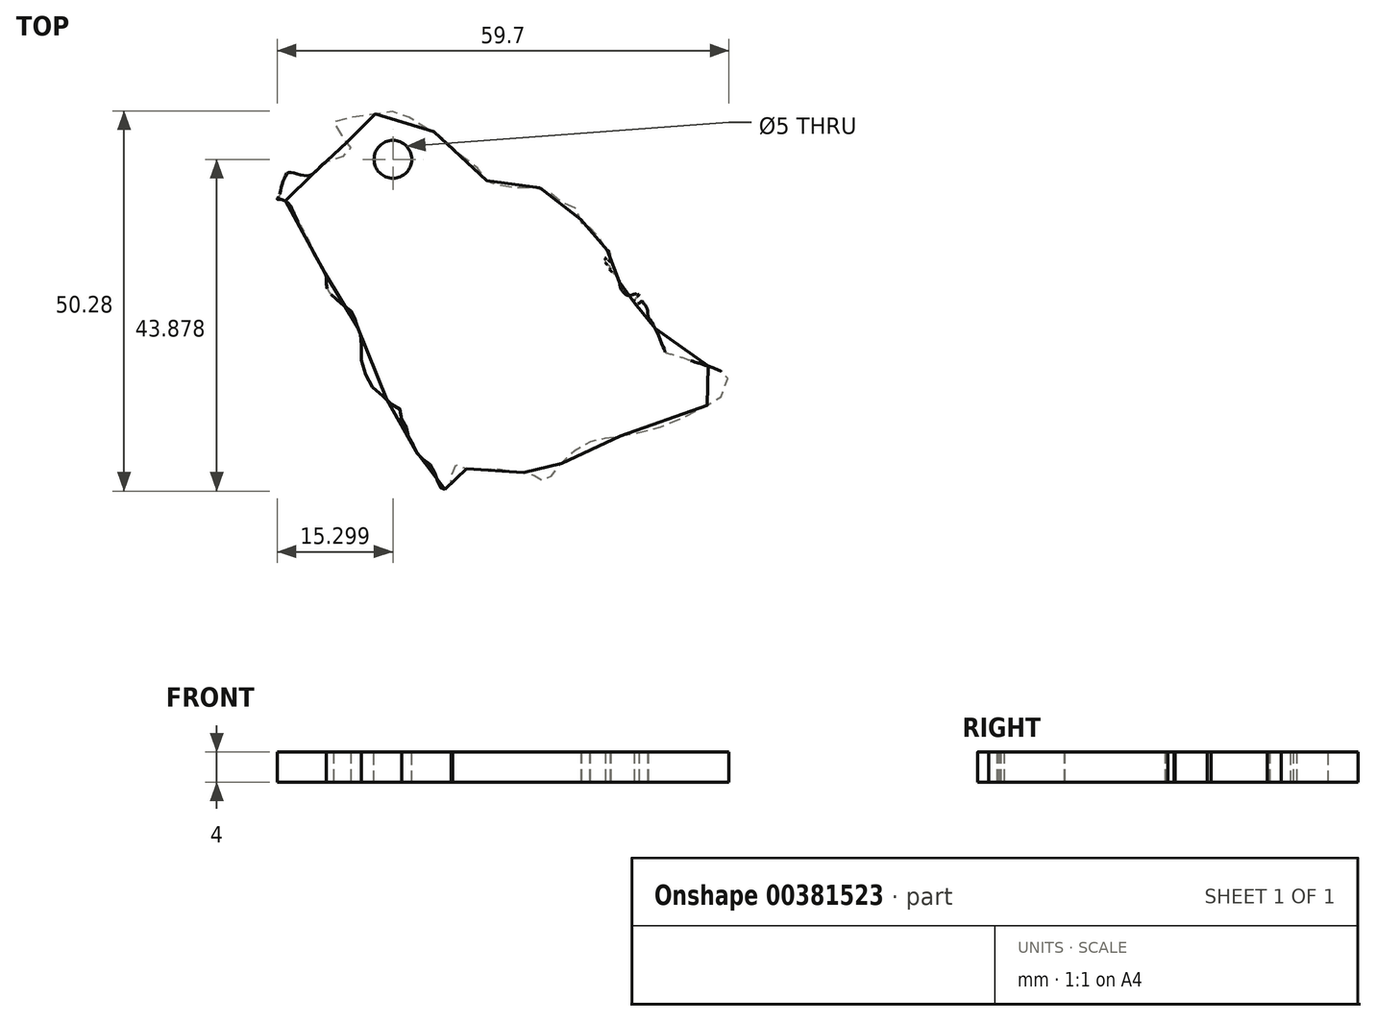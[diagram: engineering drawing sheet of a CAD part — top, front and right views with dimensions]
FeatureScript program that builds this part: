
annotation { "Feature Type Name" : "Feature", "Feature Type Description" : "" }
export const myFeature = defineFeature(function(context is Context, id is Id, definition is map)
    precondition{}
    {
        {
            var Q0;
            Q0=qCreatedBy(makeId("Top.planeOp"),FACE);
            var sketch = newSketch(context, id + "F0", { "sketchPlane" : qUnion([Q0])});
            skLineSegment(sketch, "E0", {"start": v(31.35, 26.38) * mm, "end": v(-28.65, -24.1) * mm, "construction": true});
            skFitSpline(sketch, "E1", {"points": [v(-6.3, -23.73) * mm, v(-6.16, -23.58) * mm, v(-6, -23.43) * mm, v(-5.79, -23.35) * mm, v(-5.6, -23.24) * mm, v(-5.48, -23.15) * mm, v(-5.57, -22.91) * mm, v(-5.62, -22.62) * mm, v(-5.63, -22.36) * mm, v(-5.51, -22.1) * mm, v(-5.34, -22) * mm, v(-5.37, -21.68) * mm, v(-5.4, -21.39) * mm, v(-5.37, -21.04) * mm, v(-5.27, -20.71) * mm, v(-5.05, -20.55) * mm, v(-4.8, -20.49) * mm, v(-4.56, -20.5) * mm, v(-4.28, -20.6) * mm, v(-3.95, -20.76) * mm, v(-3.66, -20.91) * mm, v(-3.34, -21.03) * mm, v(-2.93, -21.12) * mm, v(-2.37, -21.15) * mm, v(-1.75, -21.1) * mm, v(-1.23, -21.01) * mm, v(-0.67, -21) * mm, v(-0.25, -20.93) * mm, v(0.26, -20.95) * mm, v(0.85, -21) * mm, v(1.25, -21.08) * mm, v(1.93, -21.28) * mm, v(2.47, -21.36) * mm, v(2.88, -21.45) * mm, v(3.24, -21.44) * mm, v(3.67, -21.45) * mm, v(4.15, -21.5) * mm, v(4.52, -21.54) * mm, v(4.8, -21.58) * mm, v(5.1, -21.68) * mm, v(5.3, -21.8) * mm, v(5.6, -21.97) * mm, v(5.77, -22.08) * mm, v(5.87, -22.15) * mm, v(6, -22.23) * mm, v(6.13, -22.32) * mm, v(6.34, -22.43) * mm, v(6.59, -22.49) * mm, v(6.8, -22.5) * mm, v(7.05, -22.48) * mm, v(7.3, -22.36) * mm, v(7.6, -22.12) * mm, v(7.82, -21.88) * mm, v(8.05, -21.57) * mm, v(8.34, -21.16) * mm, v(8.86, -20.5) * mm, v(9.34, -20.02) * mm, v(9.9, -19.43) * mm, v(10.7, -18.66) * mm, v(11.79, -17.89) * mm, v(12.38, -17.61) * mm, v(12.95, -17.38) * mm, v(13.53, -17.2) * mm, v(14, -17.1) * mm, v(14.57, -17) * mm, v(15.02, -16.93) * mm, v(15.35, -16.86) * mm, v(15.89, -16.77) * mm, v(16.56, -16.7) * mm, v(16.9, -16.65) * mm, v(17.4, -16.56) * mm, v(17.75, -16.5) * mm, v(19.49, -16.2) * mm, v(20.7, -15.9) * mm, v(21.96, -15.55) * mm, v(23.1, -15.14) * mm, v(25.05, -14.28) * mm, v(26.33, -13.68) * mm, v(27.58, -13.04) * mm, v(28.64, -12.48) * mm, v(29.67, -12.08) * mm, v(30.02, -11.8) * mm, v(30.4, -11.13) * mm, v(30.69, -10.26) * mm, v(30.98, -9.29) * mm, v(31.19, -8.8) * mm, v(31.19, -8.62) * mm, v(30.94, -8.48) * mm, v(30.56, -8.31) * mm, v(30.26, -8.15) * mm, v(29.83, -7.94) * mm, v(29.5, -7.78) * mm, v(29.19, -7.66) * mm, v(28.73, -7.5) * mm, v(28.33, -7.38) * mm, v(27.85, -7.24) * mm, v(27.52, -7.11) * mm, v(27.18, -7) * mm, v(26.27, -6.74) * mm, v(25.29, -6.4) * mm, v(23.78, -5.95) * mm, v(22.84, -5.64) * mm, v(22.78, -5.51) * mm, v(22.66, -5.17) * mm, v(22.44, -4.7) * mm, v(22.14, -4.05) * mm, v(21.82, -3.17) * mm, v(21.44, -2.35) * mm, v(21.17, -1.9) * mm, v(21, -1.58) * mm, v(20.75, -1.2) * mm, v(20.52, -1.04) * mm, v(20.56, -0.68) * mm, v(20.46, -0.22) * mm, v(20.46, 0) * mm, v(20.39, 0.16) * mm, v(20.27, 0.4) * mm, v(20.19, 0.58) * mm, v(20.07, 0.68) * mm, v(20, 0.77) * mm, v(19.94, 0.9) * mm, v(19.9, 0.99) * mm, v(19.8, 1.1) * mm, v(19.73, 1.16) * mm, v(19.61, 1.13) * mm, v(19.54, 1.06) * mm, v(19.39, 0.91) * mm, v(19.2, 0.82) * mm, v(19.04, 0.78) * mm, v(18.83, 0.84) * mm, v(18.74, 0.93) * mm, v(18.71, 1.1) * mm, v(18.7, 1.3) * mm, v(18.8, 1.4) * mm, v(19.04, 1.66) * mm, v(19.17, 1.8) * mm, v(19.36, 2.06) * mm, v(19.25, 2.03) * mm, v(19.14, 2) * mm, v(19.03, 2.01) * mm, v(18.96, 2.08) * mm, v(18.94, 2.13) * mm, v(18.84, 2.14) * mm, v(18.7, 2.08) * mm, v(18.56, 2.02) * mm, v(18.38, 1.96) * mm, v(18.22, 1.93) * mm, v(18.1, 1.92) * mm, v(17.9, 1.94) * mm, v(17.65, 2.02) * mm, v(17.38, 2.24) * mm, v(17.1, 2.56) * mm, v(16.9, 2.92) * mm, v(16.82, 3.24) * mm, v(16.74, 3.75) * mm, v(16.54, 4.25) * mm, v(16.22, 4.65) * mm, v(15.76, 5.04) * mm, v(15.53, 5.27) * mm, v(15.54, 5.6) * mm, v(15.48, 5.8) * mm, v(15.19, 5.91) * mm, v(14.99, 6.18) * mm, v(14.9, 6.74) * mm, v(14.94, 6.9) * mm, v(15.14, 6.71) * mm, v(15.36, 6.51) * mm, v(15.52, 6.42) * mm, v(15.57, 6.7) * mm, v(15.59, 7.04) * mm, v(15.59, 7.34) * mm, v(15.47, 7.67) * mm, v(15.23, 7.88) * mm, v(15.04, 8.01) * mm, v(14.94, 8.12) * mm, v(14.9, 8.24) * mm, v(14.88, 8.43) * mm, v(14.83, 8.64) * mm, v(14.67, 9) * mm, v(14.27, 9.42) * mm, v(13.88, 9.8) * mm, v(13.47, 10.17) * mm, v(13.1, 10.42) * mm, v(12.88, 10.55) * mm, v(12.8, 10.63) * mm, v(12.86, 10.91) * mm, v(12.84, 11.05) * mm, v(12.76, 11.13) * mm, v(12.64, 11.16) * mm, v(12.44, 11.19) * mm, v(12.2, 11.21) * mm, v(12.05, 11.27) * mm, v(11.9, 11.35) * mm, v(11.69, 11.66) * mm, v(11.69, 12.1) * mm, v(11.53, 12.54) * mm, v(11.12, 13.04) * mm, v(10.8, 13.7) * mm, v(10.56, 14.1) * mm, v(10.43, 14.3) * mm, v(9.9, 14.3) * mm, v(9.2, 14.24) * mm, v(8.7, 14.2) * mm, v(8.17, 14.42) * mm, v(7.82, 14.83) * mm, v(7.54, 15.46) * mm, v(7.35, 15.77) * mm, v(7.1, 16) * mm, v(6.63, 16.15) * mm, v(6.03, 16.15) * mm, v(5.4, 16.15) * mm, v(4.75, 16.13) * mm, v(4.12, 16.12) * mm, v(3.57, 16.11) * mm, v(3.02, 16.12) * mm, v(2.41, 16.13) * mm, v(2.06, 16.18) * mm, v(1.56, 16.25) * mm, v(0.95, 16.43) * mm, v(0.5, 16.58) * mm, v(0.17, 16.7) * mm, v(0.06, 16.74) * mm, v(-0.08, 16.8) * mm, v(-0.3, 16.87) * mm, v(-0.5, 16.94) * mm, v(-0.7, 17) * mm, v(-0.8, 17.2) * mm, v(-0.99, 17.5) * mm, v(-1.3, 17.9) * mm, v(-1.84, 18.58) * mm, v(-2.6, 19.25) * mm, v(-3.47, 19.91) * mm, v(-4.24, 20.48) * mm, v(-5.04, 21.1) * mm, v(-5.74, 21.7) * mm, v(-6.15, 22.27) * mm, v(-6.72, 22.77) * mm, v(-7.27, 23.22) * mm, v(-7.9, 23.62) * mm, v(-8.64, 23.94) * mm, v(-9.3, 24.35) * mm, v(-9.86, 24.73) * mm, v(-10.42, 25.12) * mm, v(-11.05, 25.49) * mm, v(-11.53, 25.72) * mm, v(-12.17, 25.95) * mm, v(-12.76, 26.13) * mm, v(-13.15, 26.22) * mm, v(-13.6, 26.31) * mm, v(-14.18, 26.3) * mm, v(-14.74, 26.18) * mm, v(-15.18, 26.03) * mm, v(-15.9, 25.8) * mm, v(-16.92, 25.61) * mm, v(-18.01, 25.56) * mm, v(-18.93, 25.43) * mm, v(-19.6, 25.3) * mm, v(-20.34, 25.11) * mm, v(-20.88, 24.88) * mm, v(-21.07, 24.77) * mm, v(-20.98, 24.53) * mm, v(-20.7, 24.23) * mm, v(-20.31, 23.58) * mm, v(-20.07, 23.14) * mm, v(-19.7, 22.7) * mm, v(-19.32, 22.24) * mm, v(-19, 21.92) * mm, v(-18.87, 21.71) * mm, v(-18.78, 21.48) * mm, v(-18.76, 21.27) * mm, v(-18.85, 21.14) * mm, v(-19.07, 21) * mm, v(-19.33, 20.85) * mm, v(-19.6, 20.65) * mm, v(-19.85, 20.28) * mm, v(-20.1, 20.06) * mm, v(-20.59, 19.95) * mm, v(-21.2, 19.82) * mm, v(-21.78, 19.7) * mm, v(-22.23, 19.48) * mm, v(-22.66, 19.14) * mm, v(-23.31, 18.38) * mm, v(-23.74, 18.05) * mm, v(-24.2, 17.83) * mm, v(-24.85, 17.78) * mm, v(-25.85, 18) * mm, v(-26.6, 18.18) * mm, v(-27.07, 18.14) * mm, v(-27.38, 17.78) * mm, v(-27.66, 17.1) * mm, v(-27.99, 16.2) * mm, v(-28.15, 15.29) * mm, v(-28.41, 14.8) * mm, v(-28.49, 14.65) * mm, v(-28.26, 14.65) * mm, v(-27.98, 14.62) * mm, v(-27.63, 14.52) * mm, v(-27.22, 14.32) * mm, v(-26.68, 13.68) * mm, v(-26.3, 12.83) * mm, v(-25.83, 11.88) * mm, v(-25.15, 10.71) * mm, v(-24.52, 9.58) * mm, v(-24.05, 8.47) * mm, v(-23.5, 7.24) * mm, v(-23.02, 6.43) * mm, v(-22.59, 5.68) * mm, v(-22.13, 4.8) * mm, v(-22.01, 4.34) * mm, v(-21.98, 3.68) * mm, v(-21.96, 3.15) * mm, v(-21.66, 2.42) * mm, v(-20.9, 1.6) * mm, v(-20.14, 0.93) * mm, v(-19.4, 0.44) * mm, v(-18.75, -0.11) * mm, v(-18.51, -0.4) * mm, v(-18.3, -0.8) * mm, v(-18.21, -1.21) * mm, v(-18.16, -1.6) * mm, v(-18.02, -1.95) * mm, v(-17.8, -2.37) * mm, v(-17.56, -2.86) * mm, v(-17.45, -3.36) * mm, v(-17.38, -3.8) * mm, v(-17.35, -5.05) * mm, v(-17.38, -6.38) * mm, v(-17.22, -7.58) * mm, v(-16.64, -8.91) * mm, v(-16.07, -9.89) * mm, v(-15.31, -10.93) * mm, v(-14.42, -11.46) * mm, v(-13.76, -12.1) * mm, v(-13.2, -12.55) * mm, v(-12.87, -12.5) * mm, v(-12.23, -13.14) * mm, v(-12, -13.68) * mm, v(-12, -14.6) * mm, v(-11.7, -15.07) * mm, v(-11.43, -15.42) * mm, v(-11.34, -16.1) * mm, v(-11.25, -16.49) * mm, v(-11.04, -17) * mm, v(-10.77, -17.53) * mm, v(-10.5, -17.9) * mm, v(-10.27, -18.37) * mm, v(-10.07, -18.8) * mm, v(-9.85, -19.14) * mm, v(-9.6, -19.53) * mm, v(-9.28, -19.73) * mm, v(-8.82, -19.96) * mm, v(-8.43, -20.24) * mm, v(-8.18, -20.63) * mm, v(-7.87, -21.14) * mm, v(-7.61, -21.65) * mm, v(-7.41, -22.12) * mm, v(-7.26, -22.6) * mm, v(-7.18, -22.94) * mm, v(-7.04, -23.31) * mm, v(-6.9, -23.45) * mm, v(-6.72, -23.78) * mm, v(-6.51, -23.96) * mm, v(-6.36, -23.81) * mm, v(-6.3, -23.73) * mm]});
            skSolve(sketch);
        }
        {
            var Q0;
            Q0=makeQuery(id+"F0.imprint","IMPRINT",FACE,{"disambiguationData":[TD([[makeQuery(id+"F0.imprint","IMPRINT",EDGE,{"derivedFrom":sQuery(id+"F0.wireOp",EDGE,"E1")}),1.0]])]});
            extrude(context, id + "F1", {"entities" : qUnion([Q0]), "depth" : 4 * mm});
        }
        {
            var Q0;
            Q0=makeQuery(id+"F1.opExtrude","CAP_FACE",FACE,{"disambiguationData":[OSD([sQuery(id+"F0.wireOp",EDGE,"E1")])],"isStart":false});
            var sketch = newSketch(context, id + "F2", { "sketchPlane" : qUnion([Q0])});
            skCircle(sketch, "E2", {"center": v(-13.2, 19.92) * mm, "radius": 2.5 * mm});
            skSolve(sketch);
        }
        {
            var Q0;
            Q0=makeQuery(id+"F2.imprint","IMPRINT",FACE,{"disambiguationData":[TD([[makeQuery(id+"F2.imprint","IMPRINT",EDGE,{"derivedFrom":sQuery(id+"F2.wireOp",EDGE,"E2")}),1.0]])]});
            extrude(context, id + "F3", {"entities" : qUnion([Q0]), "operationType" : NewBodyOperationType.REMOVE, "oppositeDirection" : true, "depth" : 25 * mm});
        }
    });
